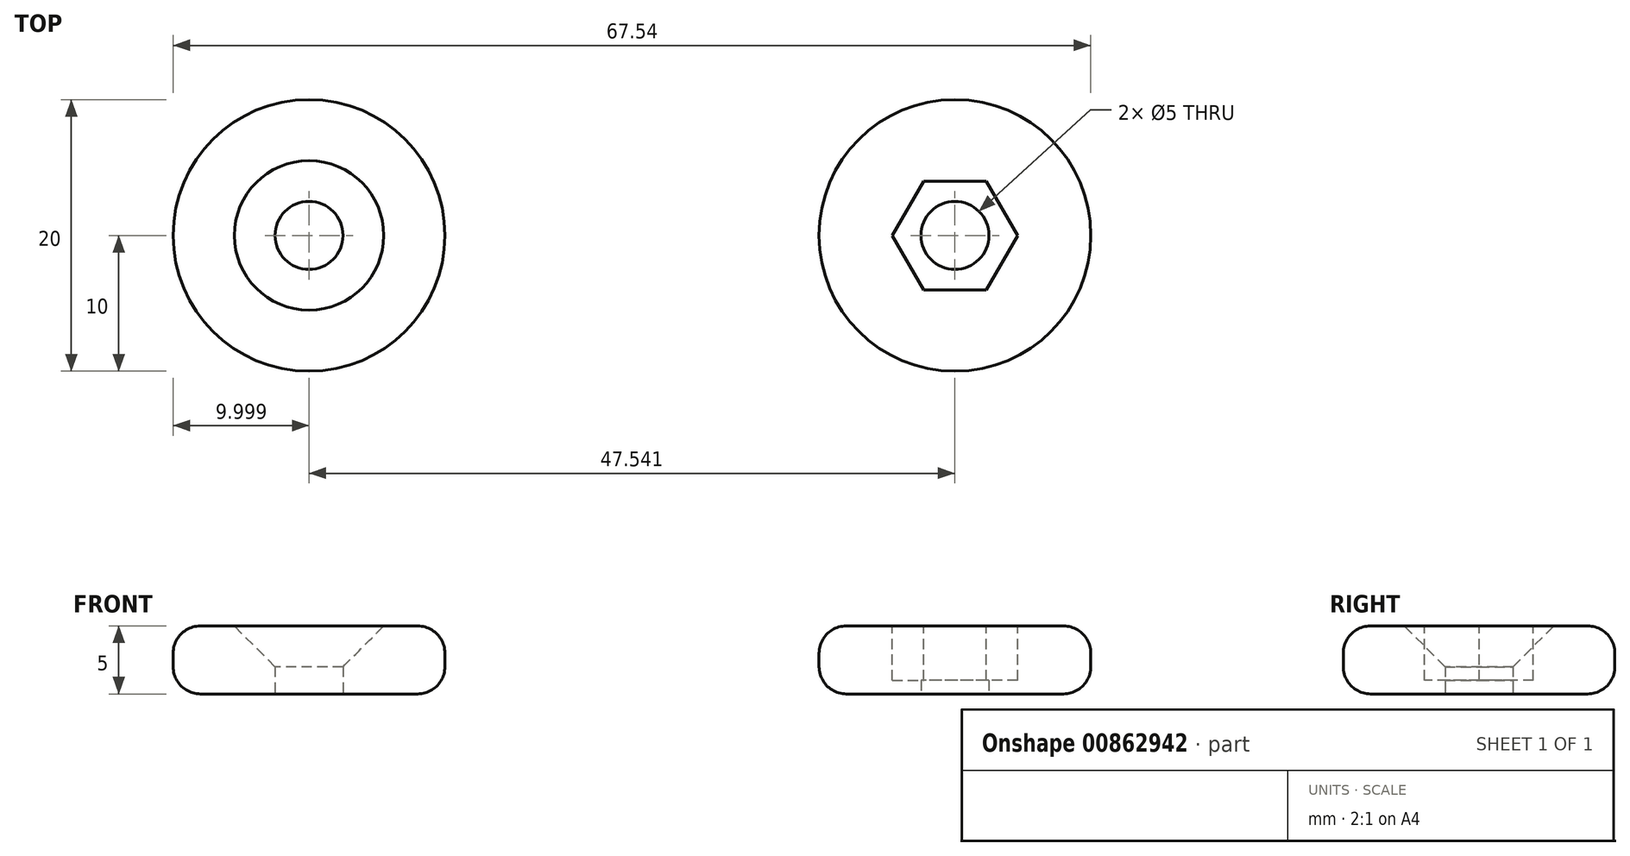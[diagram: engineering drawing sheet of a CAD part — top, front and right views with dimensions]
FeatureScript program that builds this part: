
annotation { "Feature Type Name" : "Feature", "Feature Type Description" : "" }
export const myFeature = defineFeature(function(context is Context, id is Id, definition is map)
    precondition{}
    {
        {
            var Q0;
            Q0=qCreatedBy(makeId("Top.planeOp"),FACE);
            var sketch = newSketch(context, id + "F0", { "sketchPlane" : qUnion([Q0])});
            skCircle(sketch, "E0", {"center": v(0, 0) * mm, "radius": 10 * mm});
            skCircle(sketch, "E1", {"center": v(-47.54, 0) * mm, "radius": 10 * mm});
            skCircle(sketch, "E2", {"center": v(-47.54, 0) * mm, "radius": 2.5 * mm});
            skCircle(sketch, "E3", {"center": v(0, 0) * mm, "radius": 2.5 * mm});
            skSolve(sketch);
        }
        {
            var Q0;
            Q0=makeQuery(id+"F0.imprint","IMPRINT",FACE,{"disambiguationData":[TD([[makeQuery(id+"F0.imprint","IMPRINT",EDGE,{"derivedFrom":sQuery(id+"F0.wireOp",EDGE,"E1")}),1.0]])]});
            var Q1;
            Q1=makeQuery(id+"F0.imprint","IMPRINT",FACE,{"disambiguationData":[TD([[makeQuery(id+"F0.imprint","IMPRINT",EDGE,{"derivedFrom":sQuery(id+"F0.wireOp",EDGE,"E0")}),1.0]])]});
            extrude(context, id + "F1", {"entities" : qUnion([Q0, Q1]), "depth" : 5 * mm, "offsetDistance" : 25 * mm});
        }
        {
            var Q0;
            Q0=makeQuery(id+"F1.opExtrude","CAP_FACE",FACE,{"disambiguationData":[OSD([sQuery(id+"F0.wireOp",EDGE,"E0"),sQuery(id+"F0.wireOp",EDGE,"E3")])],"isStart":false});
            var sketch = newSketch(context, id + "F2", { "sketchPlane" : qUnion([Q0])});
            skCircle(sketch, "E4.cCircle", {"center": v(0, 0) * mm, "radius": 4 * mm, "construction": true});
            skLineSegment(sketch, "E4.0", {"start": v(2.3, -4) * mm, "end": v(-2.3, -4) * mm});
            skLineSegment(sketch, "E4.1", {"start": v(-2.3, -4) * mm, "end": v(-4.62, 0) * mm});
            skLineSegment(sketch, "E4.2", {"start": v(-4.62, 0) * mm, "end": v(-2.3, 4) * mm});
            skLineSegment(sketch, "E4.3", {"start": v(-2.3, 4) * mm, "end": v(2.3, 4) * mm});
            skLineSegment(sketch, "E4.4", {"start": v(2.3, 4) * mm, "end": v(4.62, 0) * mm});
            skLineSegment(sketch, "E4.5", {"start": v(4.62, 0) * mm, "end": v(2.3, -4) * mm});
            skPoint(sketch, "E4.0.midPoint", {"position": v(0, -4) * mm});
            skSolve(sketch);
        }
        {
            var Q0;
            Q0=makeQuery(id+"F2.imprint","IMPRINT",FACE,{"disambiguationData":[TD([[makeQuery(id+"F2.imprint","IMPRINT",EDGE,{"derivedFrom":sQuery(id+"F2.wireOp",EDGE,"E4.0")}),-1.0]])]});
            extrude(context, id + "F3", {"entities" : qUnion([Q0]), "operationType" : NewBodyOperationType.REMOVE, "oppositeDirection" : true, "depth" : 4 * mm, "offsetDistance" : 25 * mm});
        }
        {
            var Q0;
            Q0=makeQuery(id+"F1.opExtrude","CAP_EDGE",EDGE,{"disambiguationData":[OSD([sQuery(id+"F0.wireOp",EDGE,"E1")])],"isStart":true});
            var Q1;
            Q1=makeQuery(id+"F1.opExtrude","CAP_EDGE",EDGE,{"disambiguationData":[OSD([sQuery(id+"F0.wireOp",EDGE,"E1")])],"isStart":false});
            var Q2;
            Q2=makeQuery(id+"F1.opExtrude","CAP_EDGE",EDGE,{"disambiguationData":[OSD([sQuery(id+"F0.wireOp",EDGE,"E0")])],"isStart":false});
            var Q3;
            Q3=makeQuery(id+"F1.opExtrude","CAP_EDGE",EDGE,{"disambiguationData":[OSD([sQuery(id+"F0.wireOp",EDGE,"E0")])],"isStart":true});
            fillet(context, id + "F4", {"entities" : qUnion([Q0, Q1, Q2, Q3]), "radius" : 2 * mm, "tangentPropagation" : true, "allowEdgeOverflow" : false});
        }
        {
            var Q0;
            Q0=makeQuery(id+"F1.opExtrude","CAP_EDGE",EDGE,{"disambiguationData":[OSD([sQuery(id+"F0.wireOp",EDGE,"E2")])],"isStart":false});
            chamfer(context, id + "F5", {"entities" : qUnion([Q0]), "width" : 3 * mm, "tangentPropagation" : true});
        }
    });
